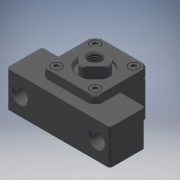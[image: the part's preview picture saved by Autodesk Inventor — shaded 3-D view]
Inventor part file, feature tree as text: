
AUTODESK INVENTOR PART (.ipt)
format: ipt  version: 2018 (Build 220112000, 112)  size: 373,248 bytes
history: native  units: mm
features: sketch x23, revolve x14, other x14, extrude x8, pattern_linear x3, thread x1, hole x1
ambient origin geometry x8: Origin, YZ Plane, XZ Plane, XY Plane, X Axis, Y Axis, Z Axis, Center Point
bodies: Solid1 (feature_tree)
feature tree (64):
  extrude  "Extrusion1"  TaperAngle=360.0deg  [1 undecoded]
  revolve  "Revolution1"  [1 undecoded]
  revolve  "Revolution2"  [1 undecoded]
  extrude  "Extrusion2"  TaperAngle=360.0deg  [1 undecoded]
  revolve  "Revolution3"  [1 undecoded]
  extrude  "Extrusion3"  TaperAngle=360.0deg  [1 undecoded]
  extrude  "Extrusion4"  Depth=20.0mm
  revolve  "Revolution4"  [1 undecoded]
  revolve  "Revolution5"  Angle=360.0deg
  thread  "Thread1"  [1 undecoded]
  revolve  "Revolution6"  [1 undecoded]
  revolve  "Revolution7"  Angle=360.0deg
  extrude  "Extrusion5"  TaperAngle=360.0deg  [1 undecoded]
  pattern_linear  "Rectangular Pattern1"  [2 undecoded]
  pattern_linear  "Rectangular Pattern2"  [2 undecoded]
  pattern_linear  "Rectangular Pattern3"  [2 undecoded]
  revolve  "Revolution8"  [1 undecoded]
  revolve  "Revolution9"  [1 undecoded]
  revolve  "Revolution10"  [1 undecoded]
  revolve  "Revolution11"  [1 undecoded]
  extrude  "Extrusion6"  [1 undecoded]
  hole  "Hole1"  [1 undecoded]
  revolve  "Revolution12"  [1 undecoded]
  extrude  "Extrusion7"  [1 undecoded]
  revolve  "Revolution13"  [1 undecoded]
  revolve  "Revolution14"  [1 undecoded]
  extrude  "Extrusion8"  [1 undecoded]
  other  "unit_XY"
  other  "unit_YZ"
  other  "unit_ZX"
  other  "unit_X"
  other  "unit_Y"
  other  "unit_Z"
  other  "unit_Center"
  other  "unit_collar_XY"
  other  "unit_collar_YZ"
  other  "unit_collar_ZX"
  other  "unit_collar_X"
  other  "unit_collar_Y"
  other  "unit_collar_Z"
  other  "unit_collar_Center"
  sketch  "Sketch_1"  dims[d0=24.0mm d1=0.0mm d2=360.0deg]
  sketch  "Sketch_3"  dims[d3=360.0deg d4=3.0mm d5=0.0mm]
  sketch  "Sketch_4"  dims[d6=360.0deg d7=8.5mm d8=0.0mm]
  sketch  "Sketch_17"  dims[d12=360.0deg d13=6.376mm d14=0.0mm]
  sketch  "Sketch_19"  dims[d25=20.0mm d27=26.162951mm d28=20.0mm d30=26.162951mm d31=20.0mm d33=26.162951mm d34=20.0mm d36=26.162951mm]
  sketch  "Sketch_18"  dims[d15=360.0deg d16=360.0deg]
  sketch  "Sketch_20"  dims[d37=360.0deg d38=360.0deg d39=360.0deg]
  sketch  "Sketch_21"  dims[d40=360.0deg d41=1.2mm d42=0.0mm]
  sketch  "Sketch_22"  dims[d43=10.0mm d44=6.0mm d45=14.5mm d46=6.0mm d47=90.0deg d48=27.5mm d49=0.0mm d50=360.0deg]
  sketch  "Sketch_24"  dims[d51=6.0mm d52=0.0mm d53=360.0deg]
  sketch  "Sketch_25"  dims[d54=360.0deg]
  sketch  "Sketch_28"  dims[d55=0.01mm d56=0.0mm]
  sketch  "Sketch_30"  dims[d57=0.0mm]
  sketch  "Sketch_31"  dims[d58=0.0mm]
  sketch  "Sketch_32"
  sketch  "Sketch_33"
  sketch  "Sketch_34"
  sketch  "Sketch18"  dims[d17=3.0mm d18=0.0mm d19=20.0mm d21=26.162951mm d22=20.0mm d24=26.162951mm]
  sketch  "Sketch_55"
  sketch  "Sketch_16"  dims[d9=3.0mm d10=0.0mm d11=360.0deg]
  sketch  "Sketch_35"
  sketch  "Sketch_50"
  sketch  "Sketch_51"
note: 27 required parameter values undecoded (feature->parameter linkage not recoverable at this tier; creation-order binding heuristic only, values carry confidence <= 0.55)